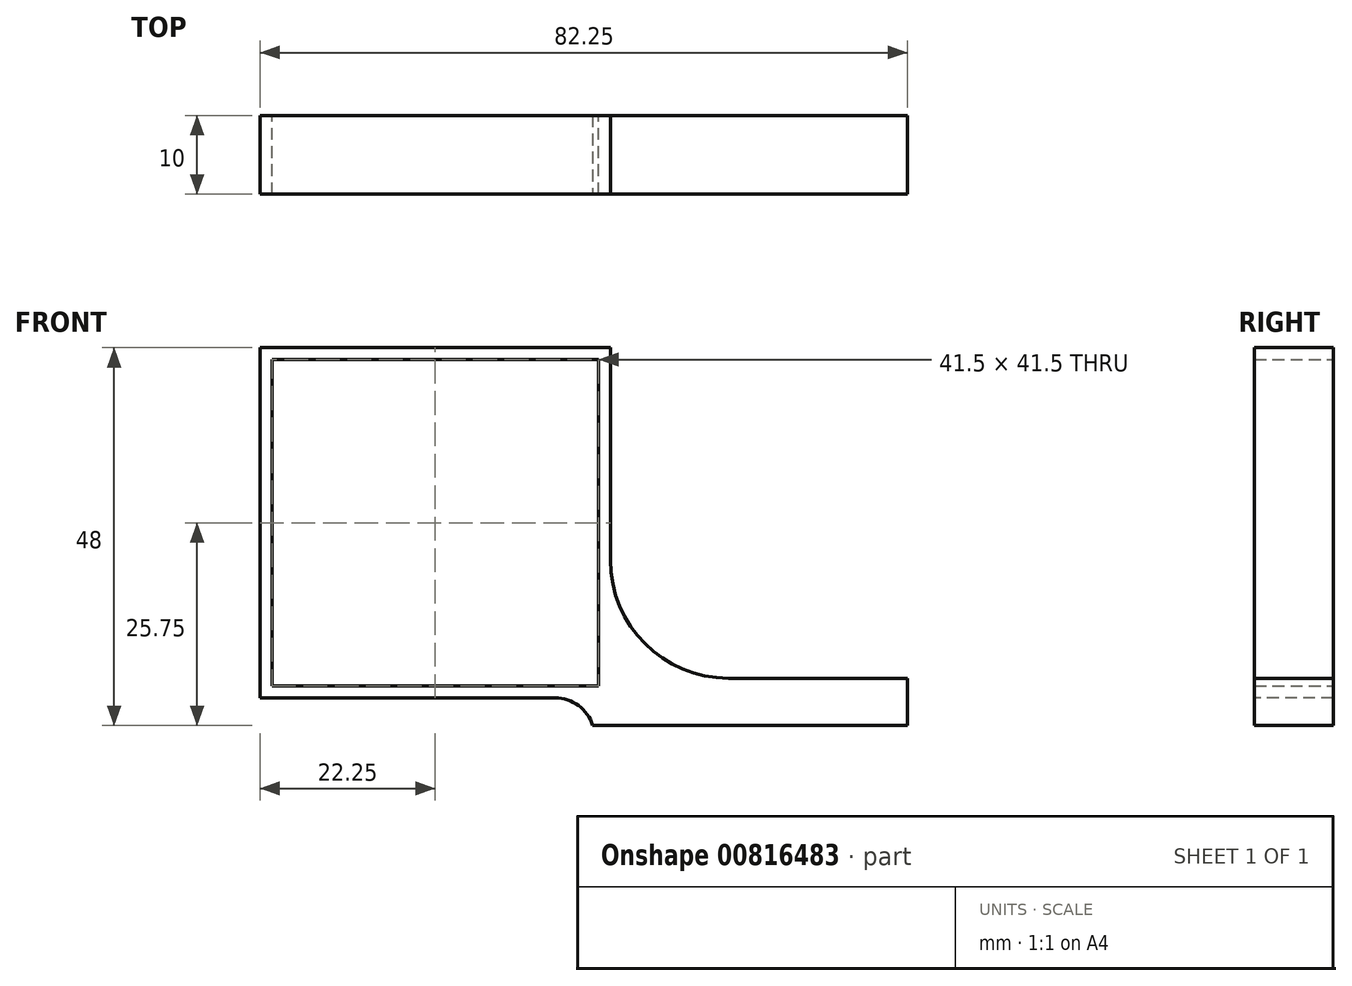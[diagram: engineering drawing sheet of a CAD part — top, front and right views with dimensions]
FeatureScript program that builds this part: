
annotation { "Feature Type Name" : "Feature", "Feature Type Description" : "" }
export const myFeature = defineFeature(function(context is Context, id is Id, definition is map)
    precondition{}
    {
        {
            var Q0;
            Q0=qCreatedBy(makeId("Front.planeOp"),FACE);
            var sketch = newSketch(context, id + "F0", { "sketchPlane" : qUnion([Q0])});
            skLineSegment(sketch, "E0.bottom", {"start": v(22.25, -22.25) * mm, "end": v(-22.25, -22.25) * mm});
            skLineSegment(sketch, "E0.top", {"start": v(22.25, 22.25) * mm, "end": v(-22.25, 22.25) * mm});
            skLineSegment(sketch, "E0.left", {"start": v(22.25, -22.25) * mm, "end": v(22.25, 22.25) * mm});
            skLineSegment(sketch, "E0.right", {"start": v(-22.25, -22.25) * mm, "end": v(-22.25, 22.25) * mm});
            skPoint(sketch, "E0.middle", {"position": v(0, 0) * mm});
            skSolve(sketch);
        }
        {
            var Q0;
            Q0 = qSketchRegion(id + "F0", true);
            extrude(context, id + "F1", {"entities" : qUnion([Q0]), "depth" : 10 * mm, "offsetDistance" : 25 * mm});
        }
        {
            var Q0;
            Q0=qCreatedBy(makeId("Front.planeOp"),FACE);
            var sketch = newSketch(context, id + "F2", { "sketchPlane" : qUnion([Q0])});
            skLineSegment(sketch, "E1.bottom", {"start": v(20.75, -20.75) * mm, "end": v(-20.75, -20.75) * mm});
            skLineSegment(sketch, "E1.top", {"start": v(20.75, 20.75) * mm, "end": v(-20.75, 20.75) * mm});
            skLineSegment(sketch, "E1.left", {"start": v(20.75, -20.75) * mm, "end": v(20.75, 20.75) * mm});
            skLineSegment(sketch, "E1.right", {"start": v(-20.75, -20.75) * mm, "end": v(-20.75, 20.75) * mm});
            skPoint(sketch, "E1.middle", {"position": v(0, 0) * mm});
            skSolve(sketch);
        }
        {
            var Q0;
            Q0 = qSketchRegion(id + "F2", true);
            extrude(context, id + "F3", {"entities" : qUnion([Q0]), "operationType" : NewBodyOperationType.REMOVE, "depth" : 10 * mm, "offsetDistance" : 25 * mm});
        }
        {
            var Q0;
            Q0=qCreatedBy(makeId("Right.planeOp"),FACE);
            var sketch = newSketch(context, id + "F4", { "sketchPlane" : qUnion([Q0])});
            skLineSegment(sketch, "E2.bottom", {"start": v(0, -19.75) * mm, "end": v(-10, -19.75) * mm});
            skLineSegment(sketch, "E2.top", {"start": v(0, -25.75) * mm, "end": v(-10, -25.75) * mm});
            skLineSegment(sketch, "E2.left", {"start": v(0, -19.75) * mm, "end": v(0, -25.75) * mm});
            skLineSegment(sketch, "E2.right", {"start": v(-10, -19.75) * mm, "end": v(-10, -25.75) * mm});
            skSolve(sketch);
        }
        {
            var Q0;
            Q0 = qSketchRegion(id + "F4", true);
            extrude(context, id + "F5", {"entities" : qUnion([Q0]), "operationType" : NewBodyOperationType.ADD, "depth" : 60 * mm, "offsetDistance" : 25 * mm, "hasSecondDirection" : true, "secondDirectionOppositeDirection" : true, "secondDirectionDepth" : -20 * mm});
        }
        {
            var Q0;
            Q0=qCreatedBy(makeId("Front.planeOp"),FACE);
            var sketch = newSketch(context, id + "F6", { "sketchPlane" : qUnion([Q0])});
            skLineSegment(sketch, "E3.bottom", {"start": v(20.75, -8.67) * mm, "end": v(1.76, -8.67) * mm});
            skLineSegment(sketch, "E3.top", {"start": v(20.75, -20.75) * mm, "end": v(1.76, -20.75) * mm});
            skLineSegment(sketch, "E3.left", {"start": v(20.75, -8.67) * mm, "end": v(20.75, -20.75) * mm});
            skLineSegment(sketch, "E3.right", {"start": v(1.76, -8.67) * mm, "end": v(1.76, -20.75) * mm});
            skSolve(sketch);
        }
        {
            var Q0;
            Q0 = qSketchRegion(id + "F6", true);
            extrude(context, id + "F7", {"entities" : qUnion([Q0]), "operationType" : NewBodyOperationType.REMOVE, "depth" : 25 * mm, "offsetDistance" : 25 * mm});
        }
        {
            var Q0;
            Q0=makeQuery(id+"F5.boolean.opBoolean","INTERSECT",EDGE,{"derivedFrom":[makeQuery(id+"F1.opExtrude","SWEPT_FACE",FACE,{"disambiguationData":[OSD([sQuery(id+"F0.wireOp",EDGE,"E0.left")])]}),makeQuery(id+"F5.opExtrude","SWEPT_FACE",FACE,{"disambiguationData":[OSD([sQuery(id+"F4.wireOp",EDGE,"E2.bottom")])]})]});
            fillet(context, id + "F8", {"entities" : qUnion([Q0]), "radius" : 15 * mm, "tangentPropagation" : true, "allowEdgeOverflow" : false});
        }
        {
            var Q0;
            Q0=makeQuery(id+"F5.boolean.opBoolean","INTERSECT",EDGE,{"derivedFrom":[makeQuery(id+"F1.opExtrude","SWEPT_FACE",FACE,{"disambiguationData":[OSD([sQuery(id+"F0.wireOp",EDGE,"E0.bottom")])]}),makeQuery(id+"F5.opExtrude","CAP_FACE",FACE,{"disambiguationData":[OSD([sQuery(id+"F4.wireOp",EDGE,"E2.bottom"),sQuery(id+"F4.wireOp",EDGE,"E2.top"),sQuery(id+"F4.wireOp",EDGE,"E2.left"),sQuery(id+"F4.wireOp",EDGE,"E2.right")])],"isStart":true})]});
            fillet(context, id + "F9", {"entities" : qUnion([Q0]), "radius" : 5 * mm, "tangentPropagation" : true, "allowEdgeOverflow" : false});
        }
    });
